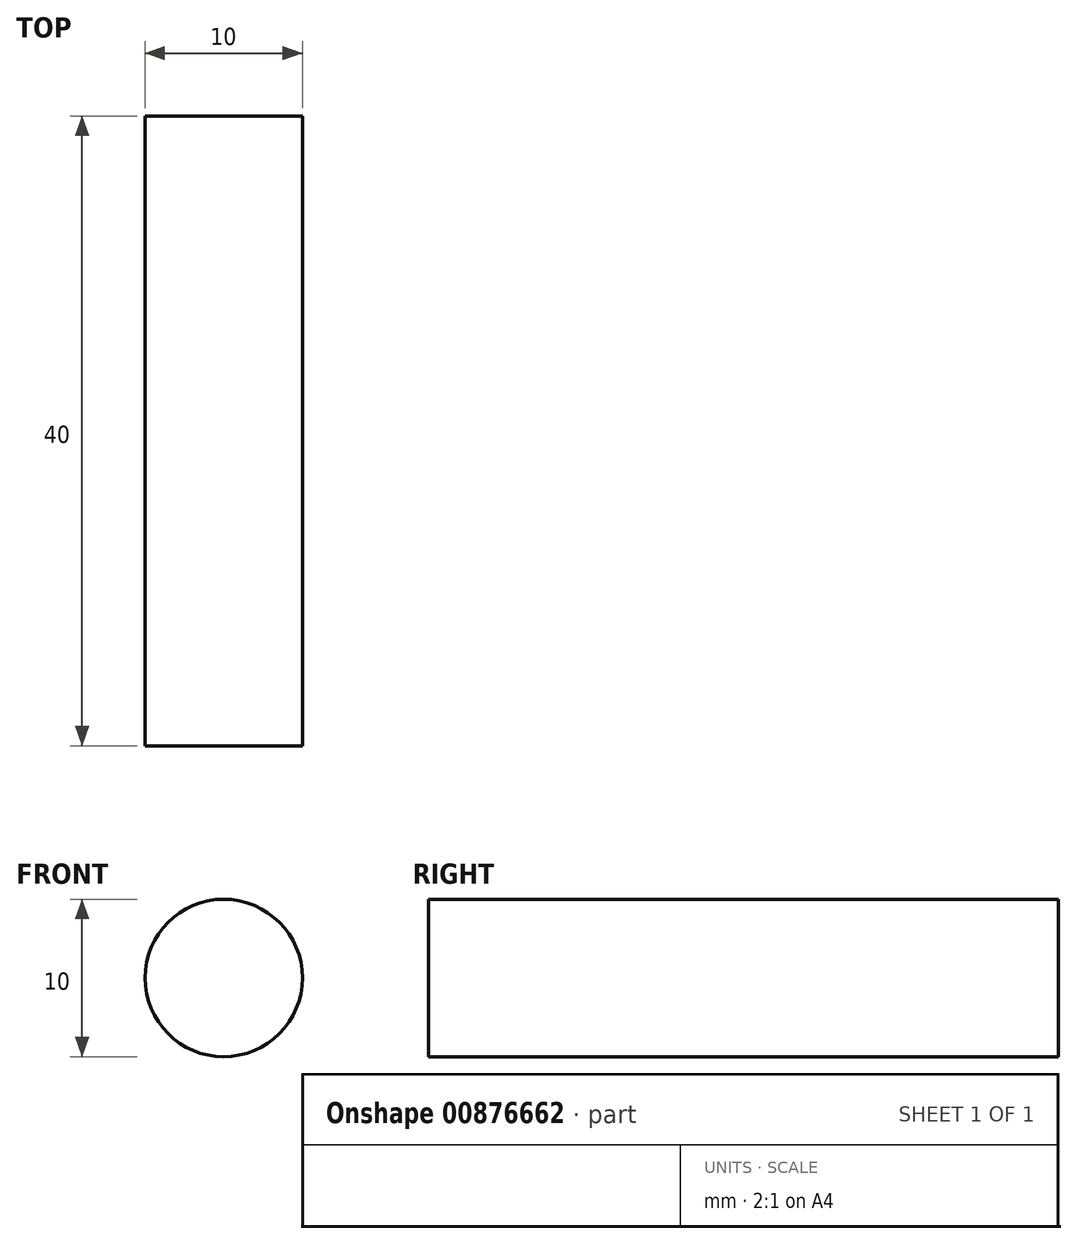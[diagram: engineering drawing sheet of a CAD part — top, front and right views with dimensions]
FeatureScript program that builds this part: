
annotation { "Feature Type Name" : "Feature", "Feature Type Description" : "" }
export const myFeature = defineFeature(function(context is Context, id is Id, definition is map)
    precondition{}
    {
        {
            var Q0;
            Q0=qCreatedBy(makeId("Front.planeOp"),FACE);
            var sketch = newSketch(context, id + "F0", { "sketchPlane" : qUnion([Q0])});
            skCircle(sketch, "E0", {"center": v(0, 0) * mm, "radius": 5 * mm});
            skSolve(sketch);
        }
        {
            var Q0;
            Q0=makeQuery(id+"F0.imprint","IMPRINT",FACE,{"disambiguationData":[TD([[makeQuery(id+"F0.imprint","IMPRINT",EDGE,{"derivedFrom":sQuery(id+"F0.wireOp",EDGE,"E0")}),-1.0]])]});
            var Q1;
            Q1=makeQuery(id+"F0.imprint","IMPRINT",FACE,{"disambiguationData":[TD([[makeQuery(id+"F0.imprint","IMPRINT",EDGE,{"derivedFrom":sQuery(id+"F0.wireOp",EDGE,"E0")}),1.0]])]});
            extrude(context, id + "F1", {"entities" : qUnion([Q0, Q1]), "depth" : 40 * mm, "offsetDistance" : 25 * mm});
        }
    });
